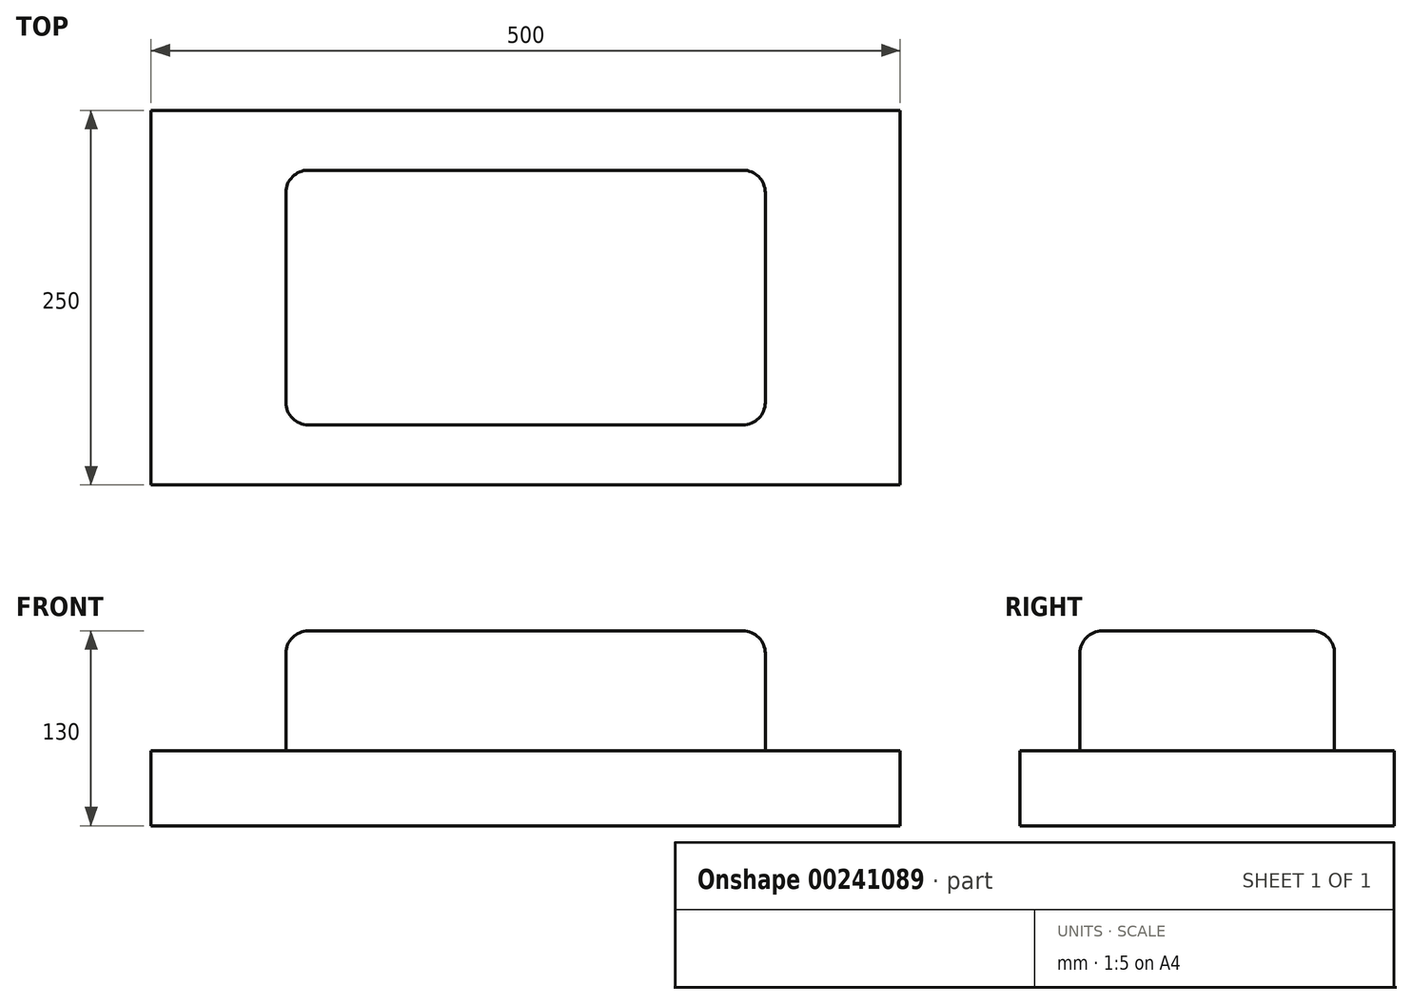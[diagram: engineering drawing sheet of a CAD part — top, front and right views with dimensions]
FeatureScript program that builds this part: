
annotation { "Feature Type Name" : "Feature", "Feature Type Description" : "" }
export const myFeature = defineFeature(function(context is Context, id is Id, definition is map)
    precondition{}
    {
        {
            var Q0;
            Q0=qCreatedBy(makeId("Top.planeOp"),FACE);
            var sketch = newSketch(context, id + "F0", { "sketchPlane" : qUnion([Q0])});
            skLineSegment(sketch, "E0.bottom", {"start": v(-250, -125) * mm, "end": v(250, -125) * mm});
            skLineSegment(sketch, "E0.top", {"start": v(-250, 125) * mm, "end": v(250, 125) * mm});
            skLineSegment(sketch, "E0.left", {"start": v(-250, -125) * mm, "end": v(-250, 125) * mm});
            skLineSegment(sketch, "E0.right", {"start": v(250, -125) * mm, "end": v(250, 125) * mm});
            skPoint(sketch, "E0.middle", {"position": v(0, 0) * mm});
            skSolve(sketch);
        }
        {
            var Q0;
            Q0=makeQuery(id+"F0.imprint","IMPRINT",FACE,{"disambiguationData":[TD([[makeQuery(id+"F0.imprint","IMPRINT",EDGE,{"derivedFrom":sQuery(id+"F0.wireOp",EDGE,"E0.bottom")}),1.0]])]});
            extrude(context, id + "F1", {"entities" : qUnion([Q0]), "endBound" : BoundingType.SYMMETRIC, "depth" : 50 * mm});
        }
        {
            var Q0;
            Q0=makeQuery(id+"F1.opExtrude","CAP_FACE",FACE,{"disambiguationData":[OSD([sQuery(id+"F0.wireOp",EDGE,"E0.bottom"),sQuery(id+"F0.wireOp",EDGE,"E0.top"),sQuery(id+"F0.wireOp",EDGE,"E0.left"),sQuery(id+"F0.wireOp",EDGE,"E0.right")])],"isStart":false});
            var sketch = newSketch(context, id + "F2", { "sketchPlane" : qUnion([Q0])});
            skLineSegment(sketch, "E1.bottom", {"start": v(-160, -85) * mm, "end": v(160, -85) * mm});
            skLineSegment(sketch, "E1.top", {"start": v(-160, 85) * mm, "end": v(160, 85) * mm});
            skLineSegment(sketch, "E1.left", {"start": v(-160, -85) * mm, "end": v(-160, 85) * mm});
            skLineSegment(sketch, "E1.right", {"start": v(160, -85) * mm, "end": v(160, 85) * mm});
            skPoint(sketch, "E1.middle", {"position": v(0, 0) * mm});
            skSolve(sketch);
        }
        {
            var Q0;
            Q0 = qSketchRegion(id + "F2", true);
            extrude(context, id + "F3", {"entities" : qUnion([Q0]), "operationType" : NewBodyOperationType.ADD, "depth" : 80 * mm});
        }
        {
            var Q0;
            Q0=makeQuery(id+"F3.opExtrude","CAP_EDGE",EDGE,{"disambiguationData":[OSD([sQuery(id+"F2.wireOp",EDGE,"E1.bottom")])],"isStart":false});
            var Q1;
            Q1=makeQuery(id+"F3.opExtrude","CAP_EDGE",EDGE,{"disambiguationData":[OSD([sQuery(id+"F2.wireOp",EDGE,"E1.left")])],"isStart":false});
            var Q2;
            Q2=makeQuery(id+"F3.opExtrude","CAP_EDGE",EDGE,{"disambiguationData":[OSD([sQuery(id+"F2.wireOp",EDGE,"E1.right")])],"isStart":false});
            var Q3;
            Q3=makeQuery(id+"F3.opExtrude","SWEPT_EDGE",EDGE,{"disambiguationData":[OSD([sQuery(id+"F2.wireOp",EDGE,"E1.bottom"),sQuery(id+"F2.wireOp",EDGE,"E1.left")])]});
            var Q4;
            Q4=makeQuery(id+"F3.opExtrude","SWEPT_EDGE",EDGE,{"disambiguationData":[OSD([sQuery(id+"F2.wireOp",EDGE,"E1.top"),sQuery(id+"F2.wireOp",EDGE,"E1.left")])]});
            var Q5;
            Q5=makeQuery(id+"F3.opExtrude","SWEPT_EDGE",EDGE,{"disambiguationData":[OSD([sQuery(id+"F2.wireOp",EDGE,"E1.bottom"),sQuery(id+"F2.wireOp",EDGE,"E1.right")])]});
            var Q6;
            Q6=makeQuery(id+"F3.opExtrude","CAP_EDGE",EDGE,{"disambiguationData":[OSD([sQuery(id+"F2.wireOp",EDGE,"E1.top")])],"isStart":false});
            var Q7;
            Q7=makeQuery(id+"F3.opExtrude","SWEPT_EDGE",EDGE,{"disambiguationData":[OSD([sQuery(id+"F2.wireOp",EDGE,"E1.top"),sQuery(id+"F2.wireOp",EDGE,"E1.right")])]});
            var Q8;
            Q8=makeQuery(id+"F3.opExtrude","CAP_EDGE",EDGE,{"disambiguationData":[OSD([sQuery(id+"F2.wireOp",EDGE,"E1.bottom")])],"isStart":true});
            fillet(context, id + "F4", {"entities" : qUnion([Q0, Q1, Q2, Q3, Q4, Q5, Q6, Q7, Q8]), "radius" : 15 * mm, "tangentPropagation" : true, "allowEdgeOverflow" : false});
        }
    });
